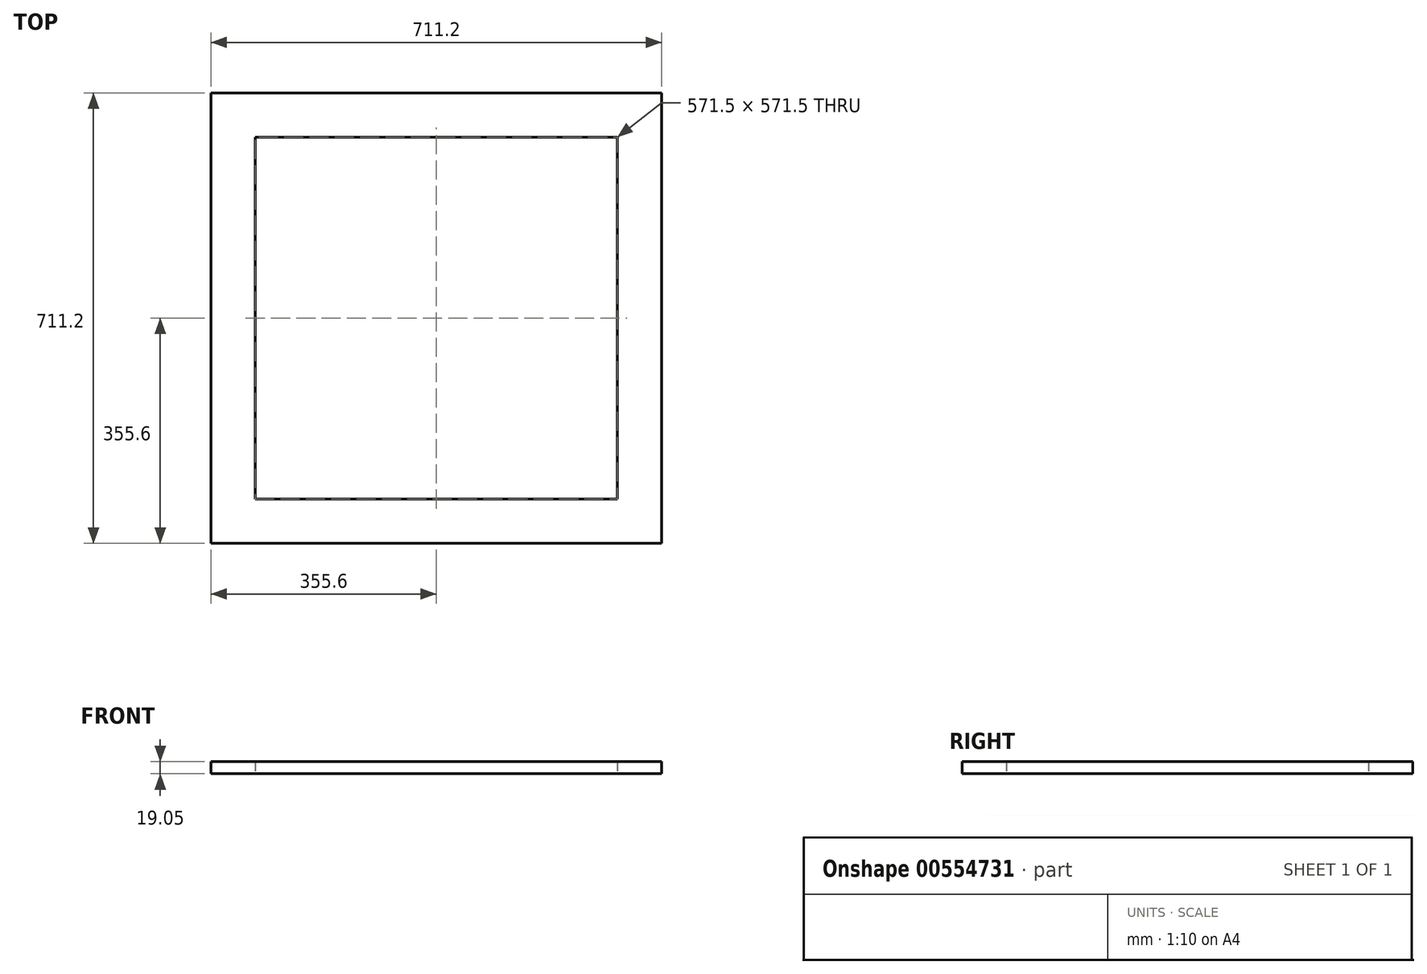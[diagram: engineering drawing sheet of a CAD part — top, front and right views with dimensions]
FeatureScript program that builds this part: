
annotation { "Feature Type Name" : "Feature", "Feature Type Description" : "" }
export const myFeature = defineFeature(function(context is Context, id is Id, definition is map)
    precondition{}
    {
        {
            var Q0;
            Q0=qCreatedBy(makeId("Top.planeOp"),FACE);
            var sketch = newSketch(context, id + "F0", { "sketchPlane" : qUnion([Q0])});
            skLineSegment(sketch, "E0.bottom", {"start": v(355.6, 355.6) * mm, "end": v(-355.6, 355.6) * mm});
            skLineSegment(sketch, "E0.top", {"start": v(355.6, -355.6) * mm, "end": v(-355.6, -355.6) * mm});
            skLineSegment(sketch, "E0.left", {"start": v(355.6, 355.6) * mm, "end": v(355.6, -355.6) * mm});
            skLineSegment(sketch, "E0.right", {"start": v(-355.6, 355.6) * mm, "end": v(-355.6, -355.6) * mm});
            skPoint(sketch, "E0.middle", {"position": v(0, 0) * mm});
            skLineSegment(sketch, "E1.bottom", {"start": v(285.75, 285.75) * mm, "end": v(-285.75, 285.75) * mm});
            skLineSegment(sketch, "E1.top", {"start": v(285.75, -285.75) * mm, "end": v(-285.75, -285.75) * mm});
            skLineSegment(sketch, "E1.left", {"start": v(285.75, 285.75) * mm, "end": v(285.75, -285.75) * mm});
            skLineSegment(sketch, "E1.right", {"start": v(-285.75, 285.75) * mm, "end": v(-285.75, -285.75) * mm});
            skSolve(sketch);
        }
        {
            var Q0;
            Q0=makeQuery(id+"F0.imprint","IMPRINT",FACE,{"disambiguationData":[TD([[makeQuery(id+"F0.imprint","IMPRINT",EDGE,{"derivedFrom":sQuery(id+"F0.wireOp",EDGE,"E0.bottom")}),1.0]])]});
            extrude(context, id + "F1", {"entities" : qUnion([Q0]), "depth" : 19.05 * mm, "offsetDistance" : 25.4 * mm});
        }
    });
